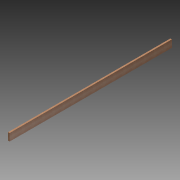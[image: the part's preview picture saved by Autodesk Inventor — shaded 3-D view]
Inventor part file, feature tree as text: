
AUTODESK INVENTOR PART (.ipt)
format: ipt  version: 2015 (Build 190159000, 159)  size: 73,728 bytes
history: native  units: in
note: dims shown in document units (in); Inventor stores cm internally (conversion verified against a paired STEP export)
features: extrude x1, sketch x1
ambient origin geometry x8: Origin, YZ Plane, XZ Plane, XY Plane, X Axis, Y Axis, Z Axis, Center Point
bodies: Solid1 (feature_tree)
feature tree (2):
  extrude  "Extrusion1"  Depth=7.25in
  sketch  "Sketch1"  dims[d0=1.5in d1=7.25in d2=160.0in d3=0.0in]
